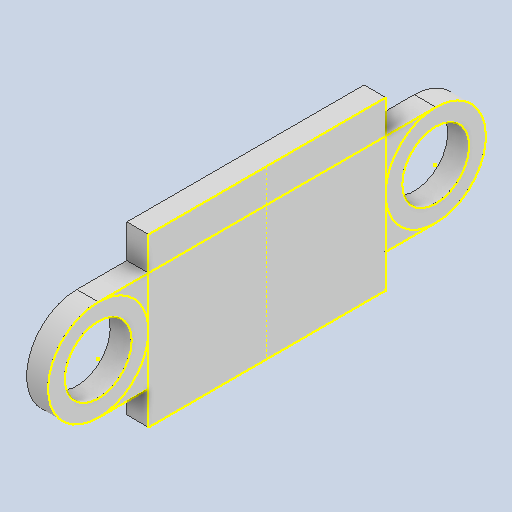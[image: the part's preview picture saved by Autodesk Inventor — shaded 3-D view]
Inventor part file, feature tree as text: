
AUTODESK INVENTOR PART (.ipt)
format: ipt  version: 2022 (Build 260153070, 153G)  size: 118,784 bytes
history: native  units: in
note: dims shown in document units (in); Inventor stores cm internally (conversion verified against a paired STEP export)
features: other x3, sketch x1
ambient origin geometry x8: Origin, YZ Plane, XZ Plane, XY Plane, X Axis, Y Axis, Z Axis, Center Point
bodies: Solid1 (feature_tree)
feature tree (4):
  other  "VL53L1X board.ipt"
  other  "Solid1::VL53L1X board.ipt"
  other  "TaggingFeature1"
  sketch  "Sketch1"  dims[d0=0.3937in]
